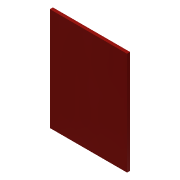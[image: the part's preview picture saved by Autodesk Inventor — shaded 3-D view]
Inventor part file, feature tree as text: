
AUTODESK INVENTOR PART (.ipt)
format: ipt  version: 2014 (Build 180170000, 170)  size: 68,608 bytes
history: native  units: mm
features: extrude x1, sketch x1
ambient origin geometry x8: Origin, YZ Plane, XZ Plane, XY Plane, X Axis, Y Axis, Z Axis, Center Point
bodies: Solid1 (feature_tree)
feature tree (2):
  extrude  "Extrusion1"  Depth=101.6mm
  sketch  "Sketch1"  dims[d0=76.2mm d1=101.6mm d2=3.0mm d3=0.0mm]
